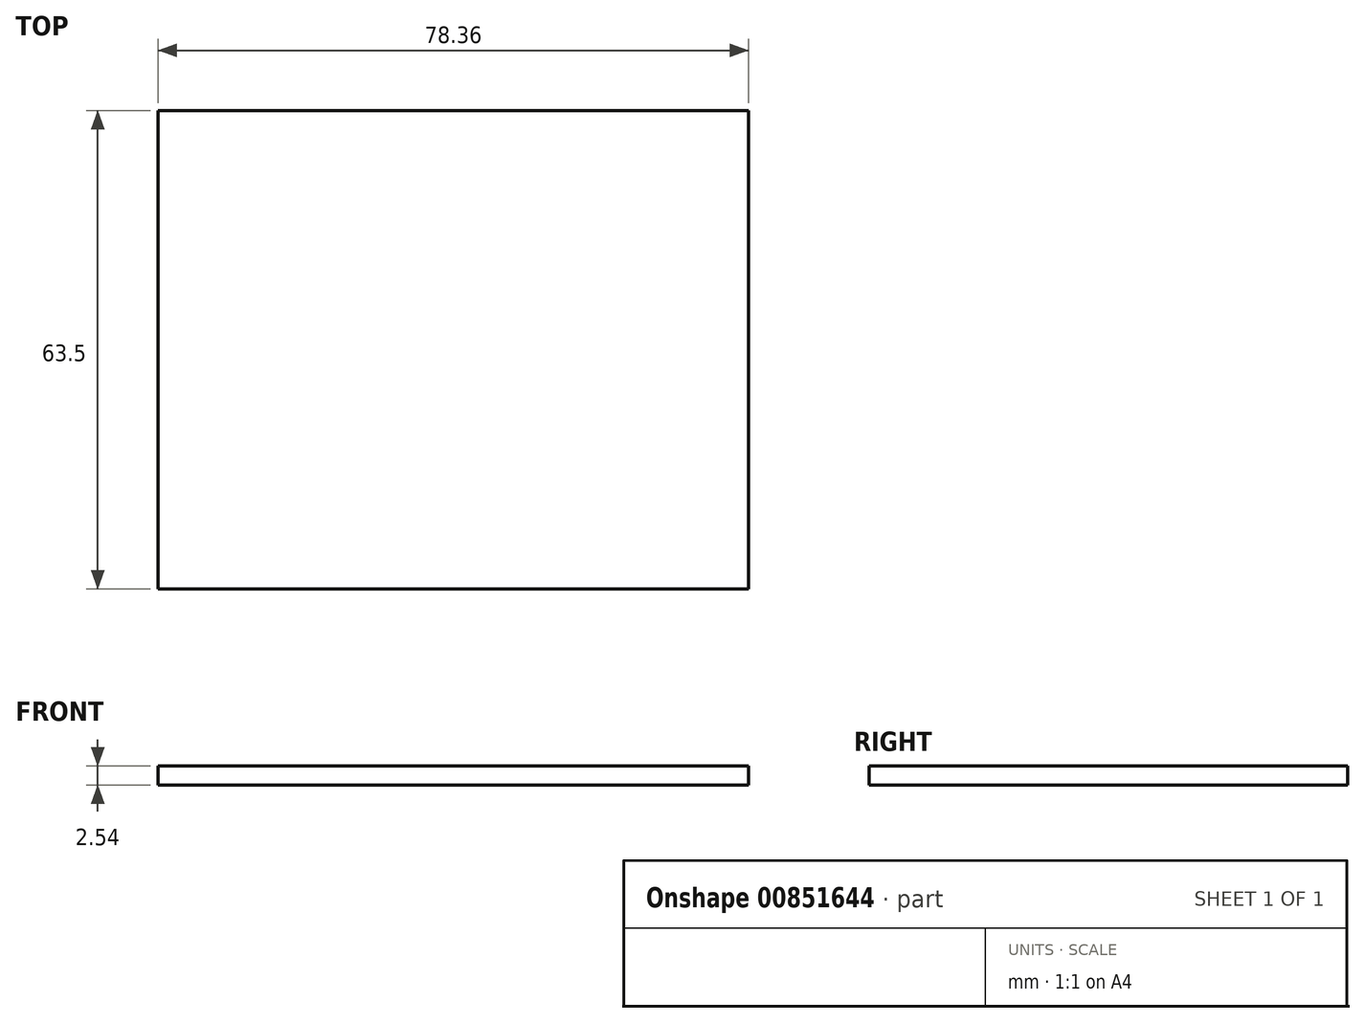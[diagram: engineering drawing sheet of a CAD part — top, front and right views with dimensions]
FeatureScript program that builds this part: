
annotation { "Feature Type Name" : "Feature", "Feature Type Description" : "" }
export const myFeature = defineFeature(function(context is Context, id is Id, definition is map)
    precondition{}
    {
        {
            var Q0;
            Q0=qCreatedBy(makeId("Front.planeOp"),FACE);
            var sketch = newSketch(context, id + "F0", { "sketchPlane" : qUnion([Q0])});
            skLineSegment(sketch, "E0.bottom", {"start": v(-35.96, 37.88) * mm, "end": v(42.4, 37.88) * mm});
            skLineSegment(sketch, "E0.top", {"start": v(-35.96, -34.86) * mm, "end": v(42.4, -34.86) * mm});
            skLineSegment(sketch, "E0.left", {"start": v(-35.96, 37.88) * mm, "end": v(-35.96, -34.86) * mm});
            skLineSegment(sketch, "E0.right", {"start": v(42.4, 37.88) * mm, "end": v(42.4, -34.86) * mm});
            skCircle(sketch, "E1", {"center": v(-13, 25.27) * mm, "radius": 10.22 * mm});
            skCircle(sketch, "E2", {"center": v(18.96, -4.68) * mm, "radius": 13.7 * mm});
            skSolve(sketch);
        }
        {
            var Q0;
            Q0=makeQuery(id+"F0.imprint","IMPRINT",FACE,{"disambiguationData":[TD([[makeQuery(id+"F0.imprint","IMPRINT",EDGE,{"derivedFrom":sQuery(id+"F0.wireOp",EDGE,"E0.bottom")}),-1.0]])]});
            var Q1;
            Q1=makeQuery(id+"F0.imprint","IMPRINT",FACE,{"disambiguationData":[TD([[makeQuery(id+"F0.imprint","IMPRINT",EDGE,{"derivedFrom":sQuery(id+"F0.wireOp",EDGE,"E2")}),1.0]])]});
            extrude(context, id + "F1", {"entities" : qUnion([Q0, Q1]), "depth" : 63.5 * mm, "offsetDistance" : 25.4 * mm, "hasDraft" : true, "draftAngle" : 0 * degree});
        }
        {
            var Q0;
            Q0=makeQuery(id+"F1.opExtrude","CAP_FACE",FACE,{"disambiguationData":[OSD([sQuery(id+"F0.wireOp",EDGE,"E0.bottom"),sQuery(id+"F0.wireOp",EDGE,"E0.top"),sQuery(id+"F0.wireOp",EDGE,"E0.left"),sQuery(id+"F0.wireOp",EDGE,"E0.right"),sQuery(id+"F0.wireOp",EDGE,"E1")])],"isStart":false});
            var Q1;
            Q1=makeQuery(id+"F1.opExtrude","SWEPT_FACE",FACE,{"disambiguationData":[OSD([sQuery(id+"F0.wireOp",EDGE,"E0.bottom")])]});
            var Q2;
            Q2=makeQuery(id+"F1.opExtrude","SWEPT_FACE",FACE,{"disambiguationData":[OSD([sQuery(id+"F0.wireOp",EDGE,"E0.left")])]});
            var Q3;
            Q3=makeQuery(id+"F1.opExtrude","SWEPT_FACE",FACE,{"disambiguationData":[OSD([sQuery(id+"F0.wireOp",EDGE,"E1")])]});
            var Q4;
            Q4=makeQuery(id+"F1.opExtrude","CAP_FACE",FACE,{"disambiguationData":[OSD([sQuery(id+"F0.wireOp",EDGE,"E0.bottom"),sQuery(id+"F0.wireOp",EDGE,"E0.top"),sQuery(id+"F0.wireOp",EDGE,"E0.left"),sQuery(id+"F0.wireOp",EDGE,"E0.right"),sQuery(id+"F0.wireOp",EDGE,"E1")])],"isStart":true});
            var Q5;
            Q5=makeQuery(id+"F1.opExtrude","SWEPT_FACE",FACE,{"disambiguationData":[OSD([sQuery(id+"F0.wireOp",EDGE,"E0.right")])]});
            shell(context, id + "F2", {"entities" : qUnion([Q0, Q1, Q2, Q3, Q4, Q5]), "thickness" : 2.54 * mm});
        }
    });
